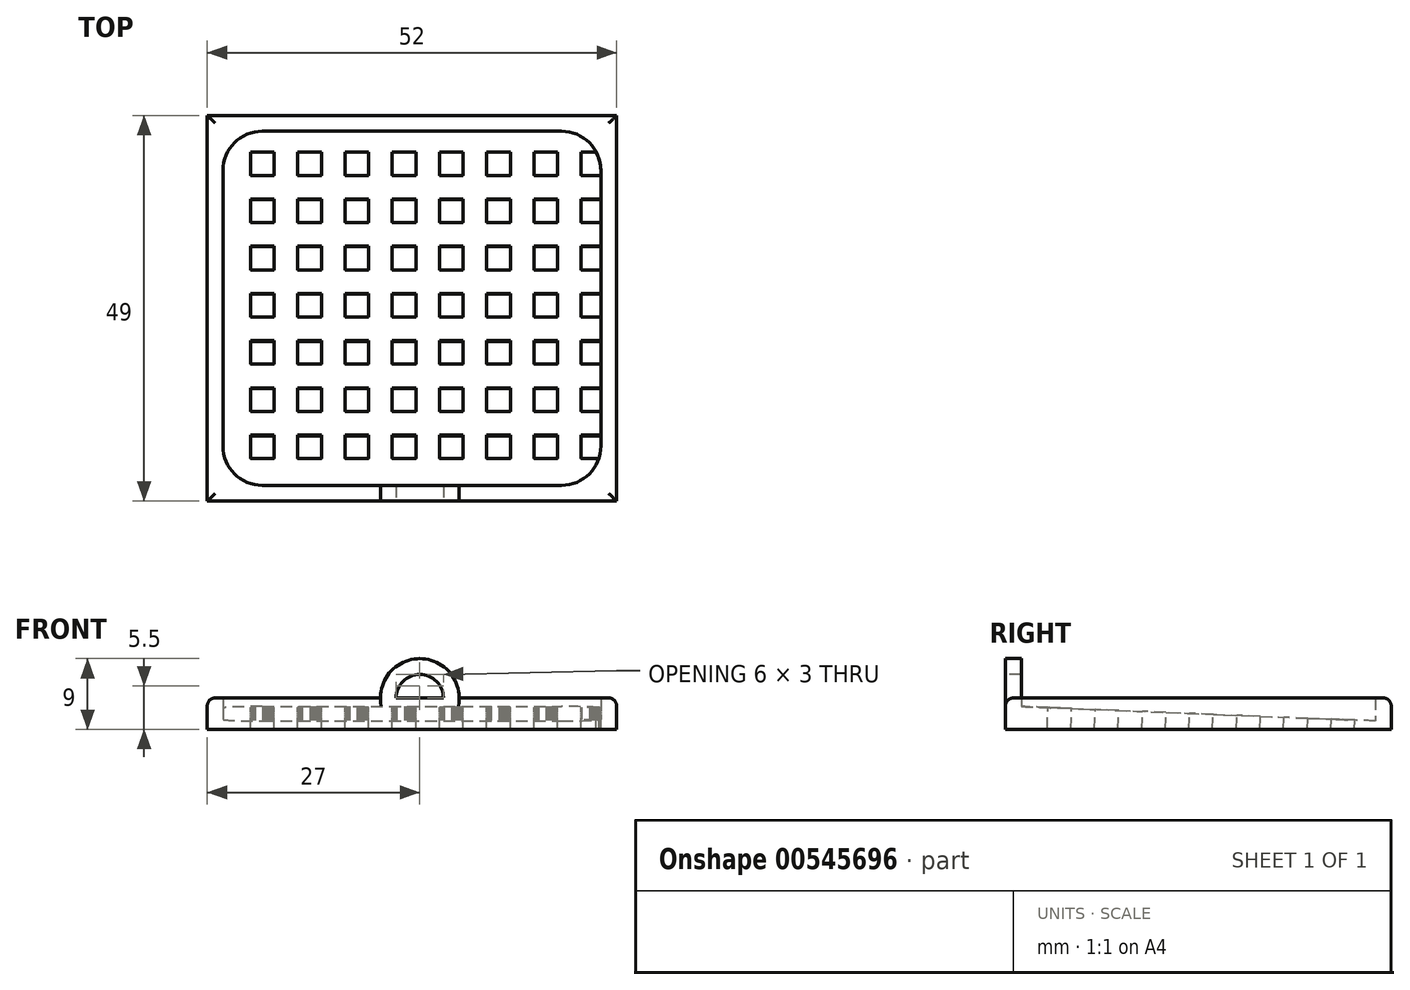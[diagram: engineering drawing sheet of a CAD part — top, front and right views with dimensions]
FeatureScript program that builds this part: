
annotation { "Feature Type Name" : "Feature", "Feature Type Description" : "" }
export const myFeature = defineFeature(function(context is Context, id is Id, definition is map)
    precondition{}
    {
        {
            var Q0;
            Q0=qCreatedBy(makeId("Top.planeOp"),FACE);
            var sketch = newSketch(context, id + "F0", { "sketchPlane" : qUnion([Q0])});
            skLineSegment(sketch, "E0.bottom", {"start": v(25, 24) * mm, "end": v(-27, 24) * mm});
            skLineSegment(sketch, "E0.top", {"start": v(25, -25) * mm, "end": v(-27, -25) * mm});
            skLineSegment(sketch, "E0.left", {"start": v(25, 24) * mm, "end": v(25, -25) * mm});
            skLineSegment(sketch, "E0.right", {"start": v(-27, 24) * mm, "end": v(-27, -25) * mm});
            skLineSegment(sketch, "E1", {"start": v(-24.88, -23) * mm, "end": v(-23.24, -21.45) * mm});
            skLineSegment(sketch, "E2.0", {"start": v(-23.42, -23) * mm, "end": v(-23.22, -22.82) * mm});
            skLineSegment(sketch, "E3.2.0.0", {"start": v(-14.88, -23) * mm, "end": v(-11.7, -20.01) * mm});
            skLineSegment(sketch, "E3.6.0.0", {"start": v(5.12, -23) * mm, "end": v(8.3, -20.01) * mm});
            skLineSegment(sketch, "E3.9.0.0", {"start": v(20.12, -23) * mm, "end": v(23, -20.29) * mm});
            skLineSegment(sketch, "E3.direction1", {"start": v(-27, -25) * mm, "end": v(-22, -25) * mm, "construction": true});
            skLineSegment(sketch, "E4.MirrorCS", {"start": v(-27, -20.37) * mm, "end": v(-26.7, -20) * mm});
            skLineSegment(sketch, "E5.MirrorCS", {"start": v(11.47, -26.5) * mm, "end": v(13.06, -25) * mm});
            skPoint(sketch, "E6.orphan", {"position": v(-24.94, 9.96) * mm});
            skPoint(sketch, "E7.orphan", {"position": v(-25.22, 4.95) * mm});
            skPoint(sketch, "E8.orphan", {"position": v(-25.54, -0.02) * mm});
            skPoint(sketch, "E9.orphan", {"position": v(28.1, 71.58) * mm});
            skPoint(sketch, "E10.orphan", {"position": v(27.67, 68.92) * mm});
            skPoint(sketch, "E11.orphan", {"position": v(27.8, 66.59) * mm});
            skPoint(sketch, "E12.orphan", {"position": v(27.37, 63.93) * mm});
            skPoint(sketch, "E13.orphan", {"position": v(27.5, 61.6) * mm});
            skPoint(sketch, "E14.orphan", {"position": v(27.08, 58.94) * mm});
            skPoint(sketch, "E15.orphan", {"position": v(27.2, 56.6) * mm});
            skPoint(sketch, "E16.orphan", {"position": v(26.78, 53.95) * mm});
            skPoint(sketch, "E17.orphan", {"position": v(26.9, 51.61) * mm});
            skPoint(sketch, "E18.orphan", {"position": v(26.48, 48.96) * mm});
            skPoint(sketch, "E19.orphan", {"position": v(26.61, 46.62) * mm});
            skPoint(sketch, "E20.orphan", {"position": v(26.19, 43.96) * mm});
            skPoint(sketch, "E21.orphan", {"position": v(28.15, 39.96) * mm});
            skPoint(sketch, "E22.orphan", {"position": v(27.44, 40.7) * mm});
            skPoint(sketch, "E23.orphan", {"position": v(27.06, 35.7) * mm});
            skPoint(sketch, "E24.orphan", {"position": v(27.77, 34.97) * mm});
            skPoint(sketch, "E25.MirrorCS.start.orphan", {"position": v(-12, -25) * mm});
            skPoint(sketch, "E26.orphan", {"position": v(45, 24) * mm});
            skPoint(sketch, "E27.orphan", {"position": v(47.68, 24.27) * mm});
            skPoint(sketch, "E28.orphan", {"position": v(50, 24) * mm});
            skPoint(sketch, "E3.5.0.0.start.orphan", {"position": v(-1.98, -25.03) * mm});
            skPoint(sketch, "E3.4.0.0.start.orphan", {"position": v(-6.99, -25.05) * mm});
            skPoint(sketch, "E29.orphan", {"position": v(52.68, 24.27) * mm});
            skPoint(sketch, "E30.orphan", {"position": v(55, 24) * mm});
            skPoint(sketch, "E31.MirrorCS.start.orphan", {"position": v(3, -25) * mm});
            skPoint(sketch, "E32.orphan", {"position": v(57.68, 24.27) * mm});
            skPoint(sketch, "E33.orphan", {"position": v(72.68, 24.27) * mm});
            skPoint(sketch, "E34.orphan", {"position": v(70, 24) * mm});
            skPoint(sketch, "E35.orphan", {"position": v(67.68, 24.27) * mm});
            skPoint(sketch, "E36.orphan", {"position": v(65, 24) * mm});
            skPoint(sketch, "E37.orphan", {"position": v(62.68, 24.27) * mm});
            skPoint(sketch, "E38.orphan", {"position": v(60, 24) * mm});
            skPoint(sketch, "E3.7.0.0.start.orphan", {"position": v(8.02, -25.02) * mm});
            skLineSegment(sketch, "E39", {"start": v(-4.84, -23) * mm, "end": v(-1.66, -19.97) * mm});
            skLineSegment(sketch, "E40.trimOffspring", {"start": v(16.63, -23) * mm, "end": v(18.34, -21.42) * mm});
            skLineSegment(sketch, "E41.trimOffspring", {"start": v(6.63, -23) * mm, "end": v(8.34, -21.42) * mm});
            skLineSegment(sketch, "E42.trimOffspring", {"start": v(-3.37, -23) * mm, "end": v(-1.66, -21.42) * mm});
            skLineSegment(sketch, "E43.trimOffspring", {"start": v(-13.37, -23) * mm, "end": v(-11.66, -21.42) * mm});
            skPoint(sketch, "E44.orphan", {"position": v(-30.63, -29.8) * mm});
            skPoint(sketch, "E45.orphan", {"position": v(-25.86, -5.02) * mm});
            skPoint(sketch, "E46.orphan", {"position": v(-26.1, -10.03) * mm});
            skPoint(sketch, "E47.orphan", {"position": v(-26.4, -15.02) * mm});
            skPoint(sketch, "E48.orphan", {"position": v(-26.7, -20) * mm});
            skLineSegment(sketch, "E49.0", {"start": v(18, 22) * mm, "end": v(-20, 22) * mm});
            skLineSegment(sketch, "E49.1", {"start": v(23, 17) * mm, "end": v(23, -18) * mm});
            skLineSegment(sketch, "E49.2", {"start": v(18, -23) * mm, "end": v(-20, -23) * mm});
            skLineSegment(sketch, "E49.3", {"start": v(-25, 17) * mm, "end": v(-25, -18) * mm});
            skPoint(sketch, "E50.orphan", {"position": v(-22, -25) * mm});
            skPoint(sketch, "E51.orphan", {"position": v(-17, -25) * mm});
            skLineSegment(sketch, "E52.trimOffspring", {"start": v(15.18, -23) * mm, "end": v(16.74, -21.53) * mm});
            skPoint(sketch, "E53.orphan", {"position": v(18, -25) * mm});
            skLineSegment(sketch, "E54.bottom", {"start": v(-11.66, 22) * mm, "end": v(-9.84, 22) * mm});
            skLineSegment(sketch, "E54.top", {"start": v(-11.66, -23) * mm, "end": v(-9.84, -23) * mm});
            skLineSegment(sketch, "E55.bottom", {"start": v(-1.66, 22) * mm, "end": v(0.21, 22) * mm});
            skLineSegment(sketch, "E55.top", {"start": v(-1.66, -23) * mm, "end": v(0.21, -23) * mm});
            skLineSegment(sketch, "E56.bottom", {"start": v(8.34, 22) * mm, "end": v(10.2, 22) * mm});
            skLineSegment(sketch, "E56.top", {"start": v(8.34, -23) * mm, "end": v(10.2, -23) * mm});
            skLineSegment(sketch, "E57.bottom", {"start": v(18.34, 22) * mm, "end": v(20.16, 22) * mm});
            skLineSegment(sketch, "E57.top", {"start": v(18.34, -23) * mm, "end": v(20.12, -23) * mm});
            skLineSegment(sketch, "E58.bottom", {"start": v(-21.63, 22) * mm, "end": v(-19.84, 22) * mm});
            skLineSegment(sketch, "E58.top", {"start": v(-21.63, -23) * mm, "end": v(-19.84, -23) * mm});
            skPoint(sketch, "E59.visualSharp", {"position": v(-25, 22) * mm});
            skArc(sketch, "E59.filletArc", {"start": v(-20, 22) * mm, "mid": v(-23.54, 20.54) * mm, "end": v(-25, 17) * mm});
            skPoint(sketch, "E60.visualSharp", {"position": v(23, 22) * mm});
            skArc(sketch, "E60.filletArc", {"start": v(23, 17) * mm, "mid": v(21.54, 20.54) * mm, "end": v(18, 22) * mm});
            skPoint(sketch, "E61.visualSharp", {"position": v(-25, -23) * mm});
            skArc(sketch, "E61.filletArc", {"start": v(-25, -18) * mm, "mid": v(-23.54, -21.54) * mm, "end": v(-20, -23) * mm});
            skPoint(sketch, "E62.visualSharp", {"position": v(23, -23) * mm});
            skArc(sketch, "E62.filletArc", {"start": v(18, -23) * mm, "mid": v(21.54, -21.54) * mm, "end": v(23, -18) * mm});
            skLineSegment(sketch, "E63.trimOffspring", {"start": v(20.16, 20.4) * mm, "end": v(21.9, 22) * mm});
            skSolve(sketch);
        }
        {
            var Q0;
            {var subQ117=sQuery(id+"F0.wireOp",EDGE,"E0.bottom");Q0=makeQuery(id+"F0.imprint","IMPRINT",FACE,{"disambiguationData":[TD([[makeQuery(id+"F0.imprint","IMPRINT",EDGE,{"derivedFrom":subQ117}),1.0]])]});}
            extrude(context, id + "F1", {"entities" : qUnion([Q0]), "depth" : 4 * mm, "offsetDistance" : 25 * mm});
        }
        {
            var Q0;
            Q0=makeQuery(id+"F1.opExtrude","SWEPT_FACE",FACE,{"disambiguationData":[OSD([sQuery(id+"F0.wireOp",EDGE,"E0.left")])]});
            var sketch = newSketch(context, id + "F2", { "sketchPlane" : qUnion([Q0])});
            skLineSegment(sketch, "E64.0.0", {"start": v(-25, 0) * mm, "end": v(24, 0) * mm});
            skLineSegment(sketch, "E64.0.1", {"start": v(24, 0) * mm, "end": v(24, 4) * mm});
            skLineSegment(sketch, "E64.0.2", {"start": v(24, 4) * mm, "end": v(-25, 4) * mm});
            skLineSegment(sketch, "E64.0.3", {"start": v(-25, 4) * mm, "end": v(-25, 0) * mm});
            skPoint(sketch, "E65", {"position": v(24, 1) * mm});
            skLineSegment(sketch, "E66", {"start": v(3.74, 1.65) * mm, "end": v(4.17, 1.62) * mm});
            skLineSegment(sketch, "E67", {"start": v(24, 0) * mm, "end": v(24, 1) * mm});
            skLineSegment(sketch, "E68", {"start": v(-25, 4) * mm, "end": v(-25, 3) * mm});
            skLineSegment(sketch, "E69", {"start": v(-25, 3) * mm, "end": v(24, 1) * mm});
            skSolve(sketch);
        }
        {
            var Q0;
            {var subQ0=sQuery(id+"F2.wireOp",EDGE,"E64.0.0");Q0=makeQuery(id+"F2.imprint","IMPRINT",FACE,{"disambiguationData":[TD([[makeQuery(id+"F2.imprint","IMPRINT",EDGE,{"derivedFrom":subQ0}),-1.0]])]});}
            extrude(context, id + "F3", {"entities" : qUnion([Q0]), "operationType" : NewBodyOperationType.ADD, "oppositeDirection" : true, "depth" : 51 * mm, "offsetDistance" : 25 * mm});
        }
        {
            var Q0;
            Q0=makeQuery(id+"F3.opExtrude","SWEPT_FACE",FACE,{"disambiguationData":[OSD([sQuery(id+"F2.wireOp",EDGE,"E69")])]});
            var sketch = newSketch(context, id + "F4", { "sketchPlane" : qUnion([Q0])});
            skLineSegment(sketch, "E70.0.0", {"start": v(-20, -23.2) * mm, "end": v(18, -23.2) * mm});
            skEllipticalArc(sketch, "E70.0.1", {});
            skLineSegment(sketch, "E70.0.2", {"start": v(23, -18.18) * mm, "end": v(23, 16.88) * mm});
            skEllipticalArc(sketch, "E70.0.3", {});
            skLineSegment(sketch, "E70.0.4", {"start": v(18, 21.9) * mm, "end": v(-20, 21.9) * mm});
            skEllipticalArc(sketch, "E70.0.5", {});
            skLineSegment(sketch, "E70.0.6", {"start": v(-25, 16.88) * mm, "end": v(-25, -18.18) * mm});
            skEllipticalArc(sketch, "E70.0.7", {});
            skLineSegment(sketch, "E71.bottom", {"start": v(-18.5, -16.68) * mm, "end": v(-21.5, -16.68) * mm});
            skLineSegment(sketch, "E71.top", {"start": v(-18.5, -19.68) * mm, "end": v(-21.5, -19.68) * mm});
            skLineSegment(sketch, "E71.left", {"start": v(-18.5, -16.68) * mm, "end": v(-18.5, -19.68) * mm});
            skLineSegment(sketch, "E71.right", {"start": v(-21.5, -16.68) * mm, "end": v(-21.5, -19.68) * mm});
            skLineSegment(sketch, "E72.0.1.0", {"start": v(-21.5, -10.68) * mm, "end": v(-21.5, -13.68) * mm});
            skLineSegment(sketch, "E72.0.1.1", {"start": v(-18.5, -10.68) * mm, "end": v(-21.5, -10.68) * mm});
            skLineSegment(sketch, "E72.0.1.2", {"start": v(-18.5, -10.68) * mm, "end": v(-18.5, -13.68) * mm});
            skLineSegment(sketch, "E72.0.1.3", {"start": v(-18.5, -13.68) * mm, "end": v(-21.5, -13.68) * mm});
            skLineSegment(sketch, "E72.0.2.0", {"start": v(-21.5, -4.68) * mm, "end": v(-21.5, -7.68) * mm});
            skLineSegment(sketch, "E72.0.2.1", {"start": v(-18.5, -4.68) * mm, "end": v(-21.5, -4.68) * mm});
            skLineSegment(sketch, "E72.0.2.2", {"start": v(-18.5, -4.68) * mm, "end": v(-18.5, -7.68) * mm});
            skLineSegment(sketch, "E72.0.2.3", {"start": v(-18.5, -7.68) * mm, "end": v(-21.5, -7.68) * mm});
            skLineSegment(sketch, "E72.0.3.0", {"start": v(-21.5, 1.32) * mm, "end": v(-21.5, -1.68) * mm});
            skLineSegment(sketch, "E72.0.3.1", {"start": v(-18.5, 1.32) * mm, "end": v(-21.5, 1.32) * mm});
            skLineSegment(sketch, "E72.0.3.2", {"start": v(-18.5, 1.32) * mm, "end": v(-18.5, -1.68) * mm});
            skLineSegment(sketch, "E72.0.3.3", {"start": v(-18.5, -1.68) * mm, "end": v(-21.5, -1.68) * mm});
            skLineSegment(sketch, "E72.0.4.0", {"start": v(-21.5, 7.32) * mm, "end": v(-21.5, 4.32) * mm});
            skLineSegment(sketch, "E72.0.4.1", {"start": v(-18.5, 7.32) * mm, "end": v(-21.5, 7.32) * mm});
            skLineSegment(sketch, "E72.0.4.2", {"start": v(-18.5, 7.32) * mm, "end": v(-18.5, 4.32) * mm});
            skLineSegment(sketch, "E72.0.4.3", {"start": v(-18.5, 4.32) * mm, "end": v(-21.5, 4.32) * mm});
            skLineSegment(sketch, "E72.0.5.0", {"start": v(-21.5, 13.32) * mm, "end": v(-21.5, 10.32) * mm});
            skLineSegment(sketch, "E72.0.5.1", {"start": v(-18.5, 13.32) * mm, "end": v(-21.5, 13.32) * mm});
            skLineSegment(sketch, "E72.0.5.2", {"start": v(-18.5, 13.32) * mm, "end": v(-18.5, 10.32) * mm});
            skLineSegment(sketch, "E72.0.5.3", {"start": v(-18.5, 10.32) * mm, "end": v(-21.5, 10.32) * mm});
            skLineSegment(sketch, "E72.0.6.0", {"start": v(-21.5, 19.32) * mm, "end": v(-21.5, 16.32) * mm});
            skLineSegment(sketch, "E72.0.6.1", {"start": v(-18.5, 19.32) * mm, "end": v(-21.5, 19.32) * mm});
            skLineSegment(sketch, "E72.0.6.2", {"start": v(-18.5, 19.32) * mm, "end": v(-18.5, 16.32) * mm});
            skLineSegment(sketch, "E72.0.6.3", {"start": v(-18.5, 16.32) * mm, "end": v(-21.5, 16.32) * mm});
            skLineSegment(sketch, "E72.1.0.0", {"start": v(-15.5, -16.68) * mm, "end": v(-15.5, -19.68) * mm});
            skLineSegment(sketch, "E72.1.0.1", {"start": v(-12.5, -16.68) * mm, "end": v(-15.5, -16.68) * mm});
            skLineSegment(sketch, "E72.1.0.2", {"start": v(-12.5, -16.68) * mm, "end": v(-12.5, -19.68) * mm});
            skLineSegment(sketch, "E72.1.0.3", {"start": v(-12.5, -19.68) * mm, "end": v(-15.5, -19.68) * mm});
            skLineSegment(sketch, "E72.1.1.0", {"start": v(-15.5, -10.68) * mm, "end": v(-15.5, -13.68) * mm});
            skLineSegment(sketch, "E72.1.1.1", {"start": v(-12.5, -10.68) * mm, "end": v(-15.5, -10.68) * mm});
            skLineSegment(sketch, "E72.1.1.2", {"start": v(-12.5, -10.68) * mm, "end": v(-12.5, -13.68) * mm});
            skLineSegment(sketch, "E72.1.1.3", {"start": v(-12.5, -13.68) * mm, "end": v(-15.5, -13.68) * mm});
            skLineSegment(sketch, "E72.1.2.0", {"start": v(-15.5, -4.68) * mm, "end": v(-15.5, -7.68) * mm});
            skLineSegment(sketch, "E72.1.2.1", {"start": v(-12.5, -4.68) * mm, "end": v(-15.5, -4.68) * mm});
            skLineSegment(sketch, "E72.1.2.2", {"start": v(-12.5, -4.68) * mm, "end": v(-12.5, -7.68) * mm});
            skLineSegment(sketch, "E72.1.2.3", {"start": v(-12.5, -7.68) * mm, "end": v(-15.5, -7.68) * mm});
            skLineSegment(sketch, "E72.1.3.0", {"start": v(-15.5, 1.32) * mm, "end": v(-15.5, -1.68) * mm});
            skLineSegment(sketch, "E72.1.3.1", {"start": v(-12.5, 1.32) * mm, "end": v(-15.5, 1.32) * mm});
            skLineSegment(sketch, "E72.1.3.2", {"start": v(-12.5, 1.32) * mm, "end": v(-12.5, -1.68) * mm});
            skLineSegment(sketch, "E72.1.3.3", {"start": v(-12.5, -1.68) * mm, "end": v(-15.5, -1.68) * mm});
            skLineSegment(sketch, "E72.1.4.0", {"start": v(-15.5, 7.32) * mm, "end": v(-15.5, 4.32) * mm});
            skLineSegment(sketch, "E72.1.4.1", {"start": v(-12.5, 7.32) * mm, "end": v(-15.5, 7.32) * mm});
            skLineSegment(sketch, "E72.1.4.2", {"start": v(-12.5, 7.32) * mm, "end": v(-12.5, 4.32) * mm});
            skLineSegment(sketch, "E72.1.4.3", {"start": v(-12.5, 4.32) * mm, "end": v(-15.5, 4.32) * mm});
            skLineSegment(sketch, "E72.1.5.0", {"start": v(-15.5, 13.32) * mm, "end": v(-15.5, 10.32) * mm});
            skLineSegment(sketch, "E72.1.5.1", {"start": v(-12.5, 13.32) * mm, "end": v(-15.5, 13.32) * mm});
            skLineSegment(sketch, "E72.1.5.2", {"start": v(-12.5, 13.32) * mm, "end": v(-12.5, 10.32) * mm});
            skLineSegment(sketch, "E72.1.5.3", {"start": v(-12.5, 10.32) * mm, "end": v(-15.5, 10.32) * mm});
            skLineSegment(sketch, "E72.1.6.0", {"start": v(-15.5, 19.32) * mm, "end": v(-15.5, 16.32) * mm});
            skLineSegment(sketch, "E72.1.6.1", {"start": v(-12.5, 19.32) * mm, "end": v(-15.5, 19.32) * mm});
            skLineSegment(sketch, "E72.1.6.2", {"start": v(-12.5, 19.32) * mm, "end": v(-12.5, 16.32) * mm});
            skLineSegment(sketch, "E72.1.6.3", {"start": v(-12.5, 16.32) * mm, "end": v(-15.5, 16.32) * mm});
            skLineSegment(sketch, "E72.2.0.0", {"start": v(-9.5, -16.68) * mm, "end": v(-9.5, -19.68) * mm});
            skLineSegment(sketch, "E72.2.0.1", {"start": v(-6.5, -16.68) * mm, "end": v(-9.5, -16.68) * mm});
            skLineSegment(sketch, "E72.2.0.2", {"start": v(-6.5, -16.68) * mm, "end": v(-6.5, -19.68) * mm});
            skLineSegment(sketch, "E72.2.0.3", {"start": v(-6.5, -19.68) * mm, "end": v(-9.5, -19.68) * mm});
            skLineSegment(sketch, "E72.2.1.0", {"start": v(-9.5, -10.68) * mm, "end": v(-9.5, -13.68) * mm});
            skLineSegment(sketch, "E72.2.1.1", {"start": v(-6.5, -10.68) * mm, "end": v(-9.5, -10.68) * mm});
            skLineSegment(sketch, "E72.2.1.2", {"start": v(-6.5, -10.68) * mm, "end": v(-6.5, -13.68) * mm});
            skLineSegment(sketch, "E72.2.1.3", {"start": v(-6.5, -13.68) * mm, "end": v(-9.5, -13.68) * mm});
            skLineSegment(sketch, "E72.2.2.0", {"start": v(-9.5, -4.68) * mm, "end": v(-9.5, -7.68) * mm});
            skLineSegment(sketch, "E72.2.2.1", {"start": v(-6.5, -4.68) * mm, "end": v(-9.5, -4.68) * mm});
            skLineSegment(sketch, "E72.2.2.2", {"start": v(-6.5, -4.68) * mm, "end": v(-6.5, -7.68) * mm});
            skLineSegment(sketch, "E72.2.2.3", {"start": v(-6.5, -7.68) * mm, "end": v(-9.5, -7.68) * mm});
            skLineSegment(sketch, "E72.2.3.0", {"start": v(-9.5, 1.32) * mm, "end": v(-9.5, -1.68) * mm});
            skLineSegment(sketch, "E72.2.3.1", {"start": v(-6.5, 1.32) * mm, "end": v(-9.5, 1.32) * mm});
            skLineSegment(sketch, "E72.2.3.2", {"start": v(-6.5, 1.32) * mm, "end": v(-6.5, -1.68) * mm});
            skLineSegment(sketch, "E72.2.3.3", {"start": v(-6.5, -1.68) * mm, "end": v(-9.5, -1.68) * mm});
            skLineSegment(sketch, "E72.2.4.0", {"start": v(-9.5, 7.32) * mm, "end": v(-9.5, 4.32) * mm});
            skLineSegment(sketch, "E72.2.4.1", {"start": v(-6.5, 7.32) * mm, "end": v(-9.5, 7.32) * mm});
            skLineSegment(sketch, "E72.2.4.2", {"start": v(-6.5, 7.32) * mm, "end": v(-6.5, 4.32) * mm});
            skLineSegment(sketch, "E72.2.4.3", {"start": v(-6.5, 4.32) * mm, "end": v(-9.5, 4.32) * mm});
            skLineSegment(sketch, "E72.2.5.0", {"start": v(-9.5, 13.32) * mm, "end": v(-9.5, 10.32) * mm});
            skLineSegment(sketch, "E72.2.5.1", {"start": v(-6.5, 13.32) * mm, "end": v(-9.5, 13.32) * mm});
            skLineSegment(sketch, "E72.2.5.2", {"start": v(-6.5, 13.32) * mm, "end": v(-6.5, 10.32) * mm});
            skLineSegment(sketch, "E72.2.5.3", {"start": v(-6.5, 10.32) * mm, "end": v(-9.5, 10.32) * mm});
            skLineSegment(sketch, "E72.2.6.0", {"start": v(-9.5, 19.32) * mm, "end": v(-9.5, 16.32) * mm});
            skLineSegment(sketch, "E72.2.6.1", {"start": v(-6.5, 19.32) * mm, "end": v(-9.5, 19.32) * mm});
            skLineSegment(sketch, "E72.2.6.2", {"start": v(-6.5, 19.32) * mm, "end": v(-6.5, 16.32) * mm});
            skLineSegment(sketch, "E72.2.6.3", {"start": v(-6.5, 16.32) * mm, "end": v(-9.5, 16.32) * mm});
            skLineSegment(sketch, "E72.3.0.0", {"start": v(-3.5, -16.68) * mm, "end": v(-3.5, -19.68) * mm});
            skLineSegment(sketch, "E72.3.0.1", {"start": v(-0.5, -16.68) * mm, "end": v(-3.5, -16.68) * mm});
            skLineSegment(sketch, "E72.3.0.2", {"start": v(-0.5, -16.68) * mm, "end": v(-0.5, -19.68) * mm});
            skLineSegment(sketch, "E72.3.0.3", {"start": v(-0.5, -19.68) * mm, "end": v(-3.5, -19.68) * mm});
            skLineSegment(sketch, "E72.3.1.0", {"start": v(-3.5, -10.68) * mm, "end": v(-3.5, -13.68) * mm});
            skLineSegment(sketch, "E72.3.1.1", {"start": v(-0.5, -10.68) * mm, "end": v(-3.5, -10.68) * mm});
            skLineSegment(sketch, "E72.3.1.2", {"start": v(-0.5, -10.68) * mm, "end": v(-0.5, -13.68) * mm});
            skLineSegment(sketch, "E72.3.1.3", {"start": v(-0.5, -13.68) * mm, "end": v(-3.5, -13.68) * mm});
            skLineSegment(sketch, "E72.3.2.0", {"start": v(-3.5, -4.68) * mm, "end": v(-3.5, -7.68) * mm});
            skLineSegment(sketch, "E72.3.2.1", {"start": v(-0.5, -4.68) * mm, "end": v(-3.5, -4.68) * mm});
            skLineSegment(sketch, "E72.3.2.2", {"start": v(-0.5, -4.68) * mm, "end": v(-0.5, -7.68) * mm});
            skLineSegment(sketch, "E72.3.2.3", {"start": v(-0.5, -7.68) * mm, "end": v(-3.5, -7.68) * mm});
            skLineSegment(sketch, "E72.3.3.0", {"start": v(-3.5, 1.32) * mm, "end": v(-3.5, -1.68) * mm});
            skLineSegment(sketch, "E72.3.3.1", {"start": v(-0.5, 1.32) * mm, "end": v(-3.5, 1.32) * mm});
            skLineSegment(sketch, "E72.3.3.2", {"start": v(-0.5, 1.32) * mm, "end": v(-0.5, -1.68) * mm});
            skLineSegment(sketch, "E72.3.3.3", {"start": v(-0.5, -1.68) * mm, "end": v(-3.5, -1.68) * mm});
            skLineSegment(sketch, "E72.3.4.0", {"start": v(-3.5, 7.32) * mm, "end": v(-3.5, 4.32) * mm});
            skLineSegment(sketch, "E72.3.4.1", {"start": v(-0.5, 7.32) * mm, "end": v(-3.5, 7.32) * mm});
            skLineSegment(sketch, "E72.3.4.2", {"start": v(-0.5, 7.32) * mm, "end": v(-0.5, 4.32) * mm});
            skLineSegment(sketch, "E72.3.4.3", {"start": v(-0.5, 4.32) * mm, "end": v(-3.5, 4.32) * mm});
            skLineSegment(sketch, "E72.3.5.0", {"start": v(-3.5, 13.32) * mm, "end": v(-3.5, 10.32) * mm});
            skLineSegment(sketch, "E72.3.5.1", {"start": v(-0.5, 13.32) * mm, "end": v(-3.5, 13.32) * mm});
            skLineSegment(sketch, "E72.3.5.2", {"start": v(-0.5, 13.32) * mm, "end": v(-0.5, 10.32) * mm});
            skLineSegment(sketch, "E72.3.5.3", {"start": v(-0.5, 10.32) * mm, "end": v(-3.5, 10.32) * mm});
            skLineSegment(sketch, "E72.3.6.0", {"start": v(-3.5, 19.32) * mm, "end": v(-3.5, 16.32) * mm});
            skLineSegment(sketch, "E72.3.6.1", {"start": v(-0.5, 19.32) * mm, "end": v(-3.5, 19.32) * mm});
            skLineSegment(sketch, "E72.3.6.2", {"start": v(-0.5, 19.32) * mm, "end": v(-0.5, 16.32) * mm});
            skLineSegment(sketch, "E72.3.6.3", {"start": v(-0.5, 16.32) * mm, "end": v(-3.5, 16.32) * mm});
            skLineSegment(sketch, "E72.4.0.0", {"start": v(2.5, -16.68) * mm, "end": v(2.5, -19.68) * mm});
            skLineSegment(sketch, "E72.4.0.1", {"start": v(5.5, -16.68) * mm, "end": v(2.5, -16.68) * mm});
            skLineSegment(sketch, "E72.4.0.2", {"start": v(5.5, -16.68) * mm, "end": v(5.5, -19.68) * mm});
            skLineSegment(sketch, "E72.4.0.3", {"start": v(5.5, -19.68) * mm, "end": v(2.5, -19.68) * mm});
            skLineSegment(sketch, "E72.4.1.0", {"start": v(2.5, -10.68) * mm, "end": v(2.5, -13.68) * mm});
            skLineSegment(sketch, "E72.4.1.1", {"start": v(5.5, -10.68) * mm, "end": v(2.5, -10.68) * mm});
            skLineSegment(sketch, "E72.4.1.2", {"start": v(5.5, -10.68) * mm, "end": v(5.5, -13.68) * mm});
            skLineSegment(sketch, "E72.4.1.3", {"start": v(5.5, -13.68) * mm, "end": v(2.5, -13.68) * mm});
            skLineSegment(sketch, "E72.4.2.0", {"start": v(2.5, -4.68) * mm, "end": v(2.5, -7.68) * mm});
            skLineSegment(sketch, "E72.4.2.1", {"start": v(5.5, -4.68) * mm, "end": v(2.5, -4.68) * mm});
            skLineSegment(sketch, "E72.4.2.2", {"start": v(5.5, -4.68) * mm, "end": v(5.5, -7.68) * mm});
            skLineSegment(sketch, "E72.4.2.3", {"start": v(5.5, -7.68) * mm, "end": v(2.5, -7.68) * mm});
            skLineSegment(sketch, "E72.4.3.0", {"start": v(2.5, 1.32) * mm, "end": v(2.5, -1.68) * mm});
            skLineSegment(sketch, "E72.4.3.1", {"start": v(5.5, 1.32) * mm, "end": v(2.5, 1.32) * mm});
            skLineSegment(sketch, "E72.4.3.2", {"start": v(5.5, 1.32) * mm, "end": v(5.5, -1.68) * mm});
            skLineSegment(sketch, "E72.4.3.3", {"start": v(5.5, -1.68) * mm, "end": v(2.5, -1.68) * mm});
            skLineSegment(sketch, "E72.4.4.0", {"start": v(2.5, 7.32) * mm, "end": v(2.5, 4.32) * mm});
            skLineSegment(sketch, "E72.4.4.1", {"start": v(5.5, 7.32) * mm, "end": v(2.5, 7.32) * mm});
            skLineSegment(sketch, "E72.4.4.2", {"start": v(5.5, 7.32) * mm, "end": v(5.5, 4.32) * mm});
            skLineSegment(sketch, "E72.4.4.3", {"start": v(5.5, 4.32) * mm, "end": v(2.5, 4.32) * mm});
            skLineSegment(sketch, "E72.4.5.0", {"start": v(2.5, 13.32) * mm, "end": v(2.5, 10.32) * mm});
            skLineSegment(sketch, "E72.4.5.1", {"start": v(5.5, 13.32) * mm, "end": v(2.5, 13.32) * mm});
            skLineSegment(sketch, "E72.4.5.2", {"start": v(5.5, 13.32) * mm, "end": v(5.5, 10.32) * mm});
            skLineSegment(sketch, "E72.4.5.3", {"start": v(5.5, 10.32) * mm, "end": v(2.5, 10.32) * mm});
            skLineSegment(sketch, "E72.4.6.0", {"start": v(2.5, 19.32) * mm, "end": v(2.5, 16.32) * mm});
            skLineSegment(sketch, "E72.4.6.1", {"start": v(5.5, 19.32) * mm, "end": v(2.5, 19.32) * mm});
            skLineSegment(sketch, "E72.4.6.2", {"start": v(5.5, 19.32) * mm, "end": v(5.5, 16.32) * mm});
            skLineSegment(sketch, "E72.4.6.3", {"start": v(5.5, 16.32) * mm, "end": v(2.5, 16.32) * mm});
            skLineSegment(sketch, "E72.5.0.0", {"start": v(8.5, -16.68) * mm, "end": v(8.5, -19.68) * mm});
            skLineSegment(sketch, "E72.5.0.1", {"start": v(11.5, -16.68) * mm, "end": v(8.5, -16.68) * mm});
            skLineSegment(sketch, "E72.5.0.2", {"start": v(11.5, -16.68) * mm, "end": v(11.5, -19.68) * mm});
            skLineSegment(sketch, "E72.5.0.3", {"start": v(11.5, -19.68) * mm, "end": v(8.5, -19.68) * mm});
            skLineSegment(sketch, "E72.5.1.0", {"start": v(8.5, -10.68) * mm, "end": v(8.5, -13.68) * mm});
            skLineSegment(sketch, "E72.5.1.1", {"start": v(11.5, -10.68) * mm, "end": v(8.5, -10.68) * mm});
            skLineSegment(sketch, "E72.5.1.2", {"start": v(11.5, -10.68) * mm, "end": v(11.5, -13.68) * mm});
            skLineSegment(sketch, "E72.5.1.3", {"start": v(11.5, -13.68) * mm, "end": v(8.5, -13.68) * mm});
            skLineSegment(sketch, "E72.5.2.0", {"start": v(8.5, -4.68) * mm, "end": v(8.5, -7.68) * mm});
            skLineSegment(sketch, "E72.5.2.1", {"start": v(11.5, -4.68) * mm, "end": v(8.5, -4.68) * mm});
            skLineSegment(sketch, "E72.5.2.2", {"start": v(11.5, -4.68) * mm, "end": v(11.5, -7.68) * mm});
            skLineSegment(sketch, "E72.5.2.3", {"start": v(11.5, -7.68) * mm, "end": v(8.5, -7.68) * mm});
            skLineSegment(sketch, "E72.5.3.0", {"start": v(8.5, 1.32) * mm, "end": v(8.5, -1.68) * mm});
            skLineSegment(sketch, "E72.5.3.1", {"start": v(11.5, 1.32) * mm, "end": v(8.5, 1.32) * mm});
            skLineSegment(sketch, "E72.5.3.2", {"start": v(11.5, 1.32) * mm, "end": v(11.5, -1.68) * mm});
            skLineSegment(sketch, "E72.5.3.3", {"start": v(11.5, -1.68) * mm, "end": v(8.5, -1.68) * mm});
            skLineSegment(sketch, "E72.5.4.0", {"start": v(8.5, 7.32) * mm, "end": v(8.5, 4.32) * mm});
            skLineSegment(sketch, "E72.5.4.1", {"start": v(11.5, 7.32) * mm, "end": v(8.5, 7.32) * mm});
            skLineSegment(sketch, "E72.5.4.2", {"start": v(11.5, 7.32) * mm, "end": v(11.5, 4.32) * mm});
            skLineSegment(sketch, "E72.5.4.3", {"start": v(11.5, 4.32) * mm, "end": v(8.5, 4.32) * mm});
            skLineSegment(sketch, "E72.5.5.0", {"start": v(8.5, 13.32) * mm, "end": v(8.5, 10.32) * mm});
            skLineSegment(sketch, "E72.5.5.1", {"start": v(11.5, 13.32) * mm, "end": v(8.5, 13.32) * mm});
            skLineSegment(sketch, "E72.5.5.2", {"start": v(11.5, 13.32) * mm, "end": v(11.5, 10.32) * mm});
            skLineSegment(sketch, "E72.5.5.3", {"start": v(11.5, 10.32) * mm, "end": v(8.5, 10.32) * mm});
            skLineSegment(sketch, "E72.5.6.0", {"start": v(8.5, 19.32) * mm, "end": v(8.5, 16.32) * mm});
            skLineSegment(sketch, "E72.5.6.1", {"start": v(11.5, 19.32) * mm, "end": v(8.5, 19.32) * mm});
            skLineSegment(sketch, "E72.5.6.2", {"start": v(11.5, 19.32) * mm, "end": v(11.5, 16.32) * mm});
            skLineSegment(sketch, "E72.5.6.3", {"start": v(11.5, 16.32) * mm, "end": v(8.5, 16.32) * mm});
            skLineSegment(sketch, "E72.6.0.0", {"start": v(14.5, -16.68) * mm, "end": v(14.5, -19.68) * mm});
            skLineSegment(sketch, "E72.6.0.1", {"start": v(17.5, -16.68) * mm, "end": v(14.5, -16.68) * mm});
            skLineSegment(sketch, "E72.6.0.2", {"start": v(17.5, -16.68) * mm, "end": v(17.5, -19.68) * mm});
            skLineSegment(sketch, "E72.6.0.3", {"start": v(17.5, -19.68) * mm, "end": v(14.5, -19.68) * mm});
            skLineSegment(sketch, "E72.6.1.0", {"start": v(14.5, -10.68) * mm, "end": v(14.5, -13.68) * mm});
            skLineSegment(sketch, "E72.6.1.1", {"start": v(17.5, -10.68) * mm, "end": v(14.5, -10.68) * mm});
            skLineSegment(sketch, "E72.6.1.2", {"start": v(17.5, -10.68) * mm, "end": v(17.5, -13.68) * mm});
            skLineSegment(sketch, "E72.6.1.3", {"start": v(17.5, -13.68) * mm, "end": v(14.5, -13.68) * mm});
            skLineSegment(sketch, "E72.6.2.0", {"start": v(14.5, -4.68) * mm, "end": v(14.5, -7.68) * mm});
            skLineSegment(sketch, "E72.6.2.1", {"start": v(17.5, -4.68) * mm, "end": v(14.5, -4.68) * mm});
            skLineSegment(sketch, "E72.6.2.2", {"start": v(17.5, -4.68) * mm, "end": v(17.5, -7.68) * mm});
            skLineSegment(sketch, "E72.6.2.3", {"start": v(17.5, -7.68) * mm, "end": v(14.5, -7.68) * mm});
            skLineSegment(sketch, "E72.6.3.0", {"start": v(14.5, 1.32) * mm, "end": v(14.5, -1.68) * mm});
            skLineSegment(sketch, "E72.6.3.1", {"start": v(17.5, 1.32) * mm, "end": v(14.5, 1.32) * mm});
            skLineSegment(sketch, "E72.6.3.2", {"start": v(17.5, 1.32) * mm, "end": v(17.5, -1.68) * mm});
            skLineSegment(sketch, "E72.6.3.3", {"start": v(17.5, -1.68) * mm, "end": v(14.5, -1.68) * mm});
            skLineSegment(sketch, "E72.6.4.0", {"start": v(14.5, 7.32) * mm, "end": v(14.5, 4.32) * mm});
            skLineSegment(sketch, "E72.6.4.1", {"start": v(17.5, 7.32) * mm, "end": v(14.5, 7.32) * mm});
            skLineSegment(sketch, "E72.6.4.2", {"start": v(17.5, 7.32) * mm, "end": v(17.5, 4.32) * mm});
            skLineSegment(sketch, "E72.6.4.3", {"start": v(17.5, 4.32) * mm, "end": v(14.5, 4.32) * mm});
            skLineSegment(sketch, "E72.6.5.0", {"start": v(14.5, 13.32) * mm, "end": v(14.5, 10.32) * mm});
            skLineSegment(sketch, "E72.6.5.1", {"start": v(17.5, 13.32) * mm, "end": v(14.5, 13.32) * mm});
            skLineSegment(sketch, "E72.6.5.2", {"start": v(17.5, 13.32) * mm, "end": v(17.5, 10.32) * mm});
            skLineSegment(sketch, "E72.6.5.3", {"start": v(17.5, 10.32) * mm, "end": v(14.5, 10.32) * mm});
            skLineSegment(sketch, "E72.6.6.0", {"start": v(14.5, 19.32) * mm, "end": v(14.5, 16.32) * mm});
            skLineSegment(sketch, "E72.6.6.1", {"start": v(17.5, 19.32) * mm, "end": v(14.5, 19.32) * mm});
            skLineSegment(sketch, "E72.6.6.2", {"start": v(17.5, 19.32) * mm, "end": v(17.5, 16.32) * mm});
            skLineSegment(sketch, "E72.6.6.3", {"start": v(17.5, 16.32) * mm, "end": v(14.5, 16.32) * mm});
            skLineSegment(sketch, "E72.7.0.0", {"start": v(20.5, -16.68) * mm, "end": v(20.5, -19.68) * mm});
            skLineSegment(sketch, "E72.7.0.1", {"start": v(23, -16.68) * mm, "end": v(20.5, -16.68) * mm});
            skLineSegment(sketch, "E72.7.0.3", {"start": v(22.77, -19.68) * mm, "end": v(20.5, -19.68) * mm});
            skLineSegment(sketch, "E72.7.1.0", {"start": v(20.5, -10.68) * mm, "end": v(20.5, -13.68) * mm});
            skLineSegment(sketch, "E72.7.1.1", {"start": v(23, -10.68) * mm, "end": v(20.5, -10.68) * mm});
            skLineSegment(sketch, "E72.7.1.3", {"start": v(23, -13.68) * mm, "end": v(20.5, -13.68) * mm});
            skLineSegment(sketch, "E72.7.2.0", {"start": v(20.5, -4.68) * mm, "end": v(20.5, -7.68) * mm});
            skLineSegment(sketch, "E72.7.2.1", {"start": v(23, -4.68) * mm, "end": v(20.5, -4.68) * mm});
            skLineSegment(sketch, "E72.7.2.3", {"start": v(23, -7.68) * mm, "end": v(20.5, -7.68) * mm});
            skLineSegment(sketch, "E72.7.3.0", {"start": v(20.5, 1.32) * mm, "end": v(20.5, -1.68) * mm});
            skLineSegment(sketch, "E72.7.3.1", {"start": v(23, 1.32) * mm, "end": v(20.5, 1.32) * mm});
            skLineSegment(sketch, "E72.7.3.3", {"start": v(23, -1.68) * mm, "end": v(20.5, -1.68) * mm});
            skLineSegment(sketch, "E72.7.4.0", {"start": v(20.5, 7.32) * mm, "end": v(20.5, 4.32) * mm});
            skLineSegment(sketch, "E72.7.4.1", {"start": v(23, 7.32) * mm, "end": v(20.5, 7.32) * mm});
            skLineSegment(sketch, "E72.7.4.3", {"start": v(23, 4.32) * mm, "end": v(20.5, 4.32) * mm});
            skLineSegment(sketch, "E72.7.5.0", {"start": v(20.5, 13.32) * mm, "end": v(20.5, 10.32) * mm});
            skLineSegment(sketch, "E72.7.5.1", {"start": v(23, 13.32) * mm, "end": v(20.5, 13.32) * mm});
            skLineSegment(sketch, "E72.7.5.3", {"start": v(23, 10.32) * mm, "end": v(20.5, 10.32) * mm});
            skLineSegment(sketch, "E72.7.6.0", {"start": v(20.5, 19.32) * mm, "end": v(20.5, 16.32) * mm});
            skLineSegment(sketch, "E72.7.6.1", {"start": v(22.37, 19.32) * mm, "end": v(20.5, 19.32) * mm});
            skLineSegment(sketch, "E72.7.6.3", {"start": v(23, 16.32) * mm, "end": v(20.5, 16.32) * mm});
            skLineSegment(sketch, "E72.direction1", {"start": v(-21.5, -19.68) * mm, "end": v(-15.5, -19.68) * mm, "construction": true});
            skLineSegment(sketch, "E72.direction2", {"start": v(-21.5, -19.68) * mm, "end": v(-21.5, -13.68) * mm, "construction": true});
            skPoint(sketch, "E73.orphan", {"position": v(23.5, -16.68) * mm});
            skPoint(sketch, "E74.orphan", {"position": v(23.5, -19.68) * mm});
            skPoint(sketch, "E75.orphan", {"position": v(23.5, -10.68) * mm});
            skPoint(sketch, "E76.orphan", {"position": v(23.5, -4.68) * mm});
            skPoint(sketch, "E77.orphan", {"position": v(23.5, 7.32) * mm});
            skPoint(sketch, "E78.orphan", {"position": v(23.5, 4.32) * mm});
            skPoint(sketch, "E79.orphan", {"position": v(23.5, 10.32) * mm});
            skPoint(sketch, "E80.orphan", {"position": v(23.5, 16.32) * mm});
            skPoint(sketch, "E81.orphan", {"position": v(23.5, 13.32) * mm});
            skPoint(sketch, "E82.orphan", {"position": v(23.5, 1.32) * mm});
            const initialGuessF4  = {"E70.0.1": [0.018, -0.01818460883017219, 0, 1, 0.005009362330054526, 0.005, 3.141592653589793, 4.71238898038469], "E70.0.3": [0.018, 0.016880927480209466, 0, 1, 0.005009362330054523, 0.005, 4.71238898038469, 0], "E70.0.5": [-0.02, 0.016880927480209463, 0, 1, 0.005009362330054526, 0.005, 0, 1.5707963267948963], "E70.0.7": [-0.02, -0.0181846088301722, 0, 1, 0.005009362330054523, 0.005, 1.5707963267948963, 3.141592653589793]};
            skSetInitialGuess(sketch, initialGuessF4);
            skSolve(sketch);
        }
        {
            var Q0;
            Q0=makeQuery(id+"F4.imprint","IMPRINT",FACE,{"disambiguationData":[TD([[makeQuery(id+"F4.imprint","IMPRINT",EDGE,{"derivedFrom":sQuery(id+"F4.wireOp",EDGE,"E72.0.6.0")}),1.0]])]});
            var Q1;
            Q1=makeQuery(id+"F4.imprint","IMPRINT",FACE,{"disambiguationData":[TD([[makeQuery(id+"F4.imprint","IMPRINT",EDGE,{"derivedFrom":sQuery(id+"F4.wireOp",EDGE,"E72.1.6.0")}),1.0]])]});
            var Q2;
            Q2=makeQuery(id+"F4.imprint","IMPRINT",FACE,{"disambiguationData":[TD([[makeQuery(id+"F4.imprint","IMPRINT",EDGE,{"derivedFrom":sQuery(id+"F4.wireOp",EDGE,"E72.2.6.0")}),1.0]])]});
            var Q3;
            Q3=makeQuery(id+"F4.imprint","IMPRINT",FACE,{"disambiguationData":[TD([[makeQuery(id+"F4.imprint","IMPRINT",EDGE,{"derivedFrom":sQuery(id+"F4.wireOp",EDGE,"E72.3.6.0")}),1.0]])]});
            var Q4;
            Q4=makeQuery(id+"F4.imprint","IMPRINT",FACE,{"disambiguationData":[TD([[makeQuery(id+"F4.imprint","IMPRINT",EDGE,{"derivedFrom":sQuery(id+"F4.wireOp",EDGE,"E72.4.6.0")}),1.0]])]});
            var Q5;
            Q5=makeQuery(id+"F4.imprint","IMPRINT",FACE,{"disambiguationData":[TD([[makeQuery(id+"F4.imprint","IMPRINT",EDGE,{"derivedFrom":sQuery(id+"F4.wireOp",EDGE,"E72.5.6.0")}),1.0]])]});
            var Q6;
            Q6=makeQuery(id+"F4.imprint","IMPRINT",FACE,{"disambiguationData":[TD([[makeQuery(id+"F4.imprint","IMPRINT",EDGE,{"derivedFrom":sQuery(id+"F4.wireOp",EDGE,"E72.6.6.0")}),1.0]])]});
            var Q7;
            Q7=makeQuery(id+"F4.imprint","IMPRINT",FACE,{"disambiguationData":[TD([[makeQuery(id+"F4.imprint","IMPRINT",EDGE,{"derivedFrom":sQuery(id+"F4.wireOp",EDGE,"E72.7.6.0")}),1.0]])]});
            var Q8;
            Q8=makeQuery(id+"F4.imprint","IMPRINT",FACE,{"disambiguationData":[TD([[makeQuery(id+"F4.imprint","IMPRINT",EDGE,{"derivedFrom":sQuery(id+"F4.wireOp",EDGE,"E72.7.5.0")}),1.0]])]});
            var Q9;
            Q9=makeQuery(id+"F4.imprint","IMPRINT",FACE,{"disambiguationData":[TD([[makeQuery(id+"F4.imprint","IMPRINT",EDGE,{"derivedFrom":sQuery(id+"F4.wireOp",EDGE,"E72.6.5.0")}),1.0]])]});
            var Q10;
            Q10=makeQuery(id+"F4.imprint","IMPRINT",FACE,{"disambiguationData":[TD([[makeQuery(id+"F4.imprint","IMPRINT",EDGE,{"derivedFrom":sQuery(id+"F4.wireOp",EDGE,"E72.5.5.0")}),1.0]])]});
            var Q11;
            Q11=makeQuery(id+"F4.imprint","IMPRINT",FACE,{"disambiguationData":[TD([[makeQuery(id+"F4.imprint","IMPRINT",EDGE,{"derivedFrom":sQuery(id+"F4.wireOp",EDGE,"E72.4.5.0")}),1.0]])]});
            var Q12;
            Q12=makeQuery(id+"F4.imprint","IMPRINT",FACE,{"disambiguationData":[TD([[makeQuery(id+"F4.imprint","IMPRINT",EDGE,{"derivedFrom":sQuery(id+"F4.wireOp",EDGE,"E72.3.5.0")}),1.0]])]});
            var Q13;
            Q13=makeQuery(id+"F4.imprint","IMPRINT",FACE,{"disambiguationData":[TD([[makeQuery(id+"F4.imprint","IMPRINT",EDGE,{"derivedFrom":sQuery(id+"F4.wireOp",EDGE,"E72.2.5.0")}),1.0]])]});
            var Q14;
            Q14=makeQuery(id+"F4.imprint","IMPRINT",FACE,{"disambiguationData":[TD([[makeQuery(id+"F4.imprint","IMPRINT",EDGE,{"derivedFrom":sQuery(id+"F4.wireOp",EDGE,"E72.1.5.0")}),1.0]])]});
            var Q15;
            Q15=makeQuery(id+"F4.imprint","IMPRINT",FACE,{"disambiguationData":[TD([[makeQuery(id+"F4.imprint","IMPRINT",EDGE,{"derivedFrom":sQuery(id+"F4.wireOp",EDGE,"E72.0.5.0")}),1.0]])]});
            var Q16;
            Q16=makeQuery(id+"F4.imprint","IMPRINT",FACE,{"disambiguationData":[TD([[makeQuery(id+"F4.imprint","IMPRINT",EDGE,{"derivedFrom":sQuery(id+"F4.wireOp",EDGE,"E72.0.4.0")}),1.0]])]});
            var Q17;
            Q17=makeQuery(id+"F4.imprint","IMPRINT",FACE,{"disambiguationData":[TD([[makeQuery(id+"F4.imprint","IMPRINT",EDGE,{"derivedFrom":sQuery(id+"F4.wireOp",EDGE,"E72.1.4.0")}),1.0]])]});
            var Q18;
            Q18=makeQuery(id+"F4.imprint","IMPRINT",FACE,{"disambiguationData":[TD([[makeQuery(id+"F4.imprint","IMPRINT",EDGE,{"derivedFrom":sQuery(id+"F4.wireOp",EDGE,"E72.2.4.0")}),1.0]])]});
            var Q19;
            Q19=makeQuery(id+"F4.imprint","IMPRINT",FACE,{"disambiguationData":[TD([[makeQuery(id+"F4.imprint","IMPRINT",EDGE,{"derivedFrom":sQuery(id+"F4.wireOp",EDGE,"E72.3.4.0")}),1.0]])]});
            var Q20;
            Q20=makeQuery(id+"F4.imprint","IMPRINT",FACE,{"disambiguationData":[TD([[makeQuery(id+"F4.imprint","IMPRINT",EDGE,{"derivedFrom":sQuery(id+"F4.wireOp",EDGE,"E72.4.4.0")}),1.0]])]});
            var Q21;
            Q21=makeQuery(id+"F4.imprint","IMPRINT",FACE,{"disambiguationData":[TD([[makeQuery(id+"F4.imprint","IMPRINT",EDGE,{"derivedFrom":sQuery(id+"F4.wireOp",EDGE,"E72.5.4.0")}),1.0]])]});
            var Q22;
            Q22=makeQuery(id+"F4.imprint","IMPRINT",FACE,{"disambiguationData":[TD([[makeQuery(id+"F4.imprint","IMPRINT",EDGE,{"derivedFrom":sQuery(id+"F4.wireOp",EDGE,"E72.6.4.0")}),1.0]])]});
            var Q23;
            Q23=makeQuery(id+"F4.imprint","IMPRINT",FACE,{"disambiguationData":[TD([[makeQuery(id+"F4.imprint","IMPRINT",EDGE,{"derivedFrom":sQuery(id+"F4.wireOp",EDGE,"E72.7.4.0")}),1.0]])]});
            var Q24;
            Q24=makeQuery(id+"F4.imprint","IMPRINT",FACE,{"disambiguationData":[TD([[makeQuery(id+"F4.imprint","IMPRINT",EDGE,{"derivedFrom":sQuery(id+"F4.wireOp",EDGE,"E72.7.3.0")}),1.0]])]});
            var Q25;
            Q25=makeQuery(id+"F4.imprint","IMPRINT",FACE,{"disambiguationData":[TD([[makeQuery(id+"F4.imprint","IMPRINT",EDGE,{"derivedFrom":sQuery(id+"F4.wireOp",EDGE,"E72.6.3.0")}),1.0]])]});
            var Q26;
            Q26=makeQuery(id+"F4.imprint","IMPRINT",FACE,{"disambiguationData":[TD([[makeQuery(id+"F4.imprint","IMPRINT",EDGE,{"derivedFrom":sQuery(id+"F4.wireOp",EDGE,"E72.5.3.0")}),1.0]])]});
            var Q27;
            Q27=makeQuery(id+"F4.imprint","IMPRINT",FACE,{"disambiguationData":[TD([[makeQuery(id+"F4.imprint","IMPRINT",EDGE,{"derivedFrom":sQuery(id+"F4.wireOp",EDGE,"E72.4.3.0")}),1.0]])]});
            var Q28;
            Q28=makeQuery(id+"F4.imprint","IMPRINT",FACE,{"disambiguationData":[TD([[makeQuery(id+"F4.imprint","IMPRINT",EDGE,{"derivedFrom":sQuery(id+"F4.wireOp",EDGE,"E72.3.3.0")}),1.0]])]});
            var Q29;
            Q29=makeQuery(id+"F4.imprint","IMPRINT",FACE,{"disambiguationData":[TD([[makeQuery(id+"F4.imprint","IMPRINT",EDGE,{"derivedFrom":sQuery(id+"F4.wireOp",EDGE,"E72.2.3.0")}),1.0]])]});
            var Q30;
            Q30=makeQuery(id+"F4.imprint","IMPRINT",FACE,{"disambiguationData":[TD([[makeQuery(id+"F4.imprint","IMPRINT",EDGE,{"derivedFrom":sQuery(id+"F4.wireOp",EDGE,"E72.1.3.0")}),1.0]])]});
            var Q31;
            Q31=makeQuery(id+"F4.imprint","IMPRINT",FACE,{"disambiguationData":[TD([[makeQuery(id+"F4.imprint","IMPRINT",EDGE,{"derivedFrom":sQuery(id+"F4.wireOp",EDGE,"E72.0.3.0")}),1.0]])]});
            var Q32;
            Q32=makeQuery(id+"F4.imprint","IMPRINT",FACE,{"disambiguationData":[TD([[makeQuery(id+"F4.imprint","IMPRINT",EDGE,{"derivedFrom":sQuery(id+"F4.wireOp",EDGE,"E72.0.2.0")}),1.0]])]});
            var Q33;
            Q33=makeQuery(id+"F4.imprint","IMPRINT",FACE,{"disambiguationData":[TD([[makeQuery(id+"F4.imprint","IMPRINT",EDGE,{"derivedFrom":sQuery(id+"F4.wireOp",EDGE,"E72.1.2.0")}),1.0]])]});
            var Q34;
            Q34=makeQuery(id+"F4.imprint","IMPRINT",FACE,{"disambiguationData":[TD([[makeQuery(id+"F4.imprint","IMPRINT",EDGE,{"derivedFrom":sQuery(id+"F4.wireOp",EDGE,"E72.2.2.0")}),1.0]])]});
            var Q35;
            Q35=makeQuery(id+"F4.imprint","IMPRINT",FACE,{"disambiguationData":[TD([[makeQuery(id+"F4.imprint","IMPRINT",EDGE,{"derivedFrom":sQuery(id+"F4.wireOp",EDGE,"E72.3.2.0")}),1.0]])]});
            var Q36;
            Q36=makeQuery(id+"F4.imprint","IMPRINT",FACE,{"disambiguationData":[TD([[makeQuery(id+"F4.imprint","IMPRINT",EDGE,{"derivedFrom":sQuery(id+"F4.wireOp",EDGE,"E72.4.2.0")}),1.0]])]});
            var Q37;
            Q37=makeQuery(id+"F4.imprint","IMPRINT",FACE,{"disambiguationData":[TD([[makeQuery(id+"F4.imprint","IMPRINT",EDGE,{"derivedFrom":sQuery(id+"F4.wireOp",EDGE,"E72.5.2.0")}),1.0]])]});
            var Q38;
            Q38=makeQuery(id+"F4.imprint","IMPRINT",FACE,{"disambiguationData":[TD([[makeQuery(id+"F4.imprint","IMPRINT",EDGE,{"derivedFrom":sQuery(id+"F4.wireOp",EDGE,"E72.6.2.0")}),1.0]])]});
            var Q39;
            Q39=makeQuery(id+"F4.imprint","IMPRINT",FACE,{"disambiguationData":[TD([[makeQuery(id+"F4.imprint","IMPRINT",EDGE,{"derivedFrom":sQuery(id+"F4.wireOp",EDGE,"E72.7.2.0")}),1.0]])]});
            var Q40;
            Q40=makeQuery(id+"F4.imprint","IMPRINT",FACE,{"disambiguationData":[TD([[makeQuery(id+"F4.imprint","IMPRINT",EDGE,{"derivedFrom":sQuery(id+"F4.wireOp",EDGE,"E72.7.1.0")}),1.0]])]});
            var Q41;
            Q41=makeQuery(id+"F4.imprint","IMPRINT",FACE,{"disambiguationData":[TD([[makeQuery(id+"F4.imprint","IMPRINT",EDGE,{"derivedFrom":sQuery(id+"F4.wireOp",EDGE,"E72.7.0.0")}),1.0]])]});
            var Q42;
            Q42=makeQuery(id+"F4.imprint","IMPRINT",FACE,{"disambiguationData":[TD([[makeQuery(id+"F4.imprint","IMPRINT",EDGE,{"derivedFrom":sQuery(id+"F4.wireOp",EDGE,"E72.6.1.0")}),1.0]])]});
            var Q43;
            Q43=makeQuery(id+"F4.imprint","IMPRINT",FACE,{"disambiguationData":[TD([[makeQuery(id+"F4.imprint","IMPRINT",EDGE,{"derivedFrom":sQuery(id+"F4.wireOp",EDGE,"E72.6.0.0")}),1.0]])]});
            var Q44;
            Q44=makeQuery(id+"F4.imprint","IMPRINT",FACE,{"disambiguationData":[TD([[makeQuery(id+"F4.imprint","IMPRINT",EDGE,{"derivedFrom":sQuery(id+"F4.wireOp",EDGE,"E72.5.0.0")}),1.0]])]});
            var Q45;
            Q45=makeQuery(id+"F4.imprint","IMPRINT",FACE,{"disambiguationData":[TD([[makeQuery(id+"F4.imprint","IMPRINT",EDGE,{"derivedFrom":sQuery(id+"F4.wireOp",EDGE,"E72.5.1.0")}),1.0]])]});
            var Q46;
            Q46=makeQuery(id+"F4.imprint","IMPRINT",FACE,{"disambiguationData":[TD([[makeQuery(id+"F4.imprint","IMPRINT",EDGE,{"derivedFrom":sQuery(id+"F4.wireOp",EDGE,"E72.4.1.0")}),1.0]])]});
            var Q47;
            Q47=makeQuery(id+"F4.imprint","IMPRINT",FACE,{"disambiguationData":[TD([[makeQuery(id+"F4.imprint","IMPRINT",EDGE,{"derivedFrom":sQuery(id+"F4.wireOp",EDGE,"E72.4.0.0")}),1.0]])]});
            var Q48;
            Q48=makeQuery(id+"F4.imprint","IMPRINT",FACE,{"disambiguationData":[TD([[makeQuery(id+"F4.imprint","IMPRINT",EDGE,{"derivedFrom":sQuery(id+"F4.wireOp",EDGE,"E72.3.0.0")}),1.0]])]});
            var Q49;
            Q49=makeQuery(id+"F4.imprint","IMPRINT",FACE,{"disambiguationData":[TD([[makeQuery(id+"F4.imprint","IMPRINT",EDGE,{"derivedFrom":sQuery(id+"F4.wireOp",EDGE,"E72.3.1.0")}),1.0]])]});
            var Q50;
            Q50=makeQuery(id+"F4.imprint","IMPRINT",FACE,{"disambiguationData":[TD([[makeQuery(id+"F4.imprint","IMPRINT",EDGE,{"derivedFrom":sQuery(id+"F4.wireOp",EDGE,"E72.2.1.0")}),1.0]])]});
            var Q51;
            Q51=makeQuery(id+"F4.imprint","IMPRINT",FACE,{"disambiguationData":[TD([[makeQuery(id+"F4.imprint","IMPRINT",EDGE,{"derivedFrom":sQuery(id+"F4.wireOp",EDGE,"E72.2.0.0")}),1.0]])]});
            var Q52;
            Q52=makeQuery(id+"F4.imprint","IMPRINT",FACE,{"disambiguationData":[TD([[makeQuery(id+"F4.imprint","IMPRINT",EDGE,{"derivedFrom":sQuery(id+"F4.wireOp",EDGE,"E72.1.0.0")}),1.0]])]});
            var Q53;
            Q53=makeQuery(id+"F4.imprint","IMPRINT",FACE,{"disambiguationData":[TD([[makeQuery(id+"F4.imprint","IMPRINT",EDGE,{"derivedFrom":sQuery(id+"F4.wireOp",EDGE,"E72.1.1.0")}),1.0]])]});
            var Q54;
            Q54=makeQuery(id+"F4.imprint","IMPRINT",FACE,{"disambiguationData":[TD([[makeQuery(id+"F4.imprint","IMPRINT",EDGE,{"derivedFrom":sQuery(id+"F4.wireOp",EDGE,"E72.0.1.0")}),1.0]])]});
            var Q55;
            Q55=makeQuery(id+"F4.imprint","IMPRINT",FACE,{"disambiguationData":[TD([[makeQuery(id+"F4.imprint","IMPRINT",EDGE,{"derivedFrom":sQuery(id+"F4.wireOp",EDGE,"E71.bottom")}),1.0]])]});
            extrude(context, id + "F5", {"entities" : qUnion([Q0, Q1, Q2, Q3, Q4, Q5, Q6, Q7, Q8, Q9, Q10, Q11, Q12, Q13, Q14, Q15, Q16, Q17, Q18, Q19, Q20, Q21, Q22, Q23, Q24, Q25, Q26, Q27, Q28, Q29, Q30, Q31, Q32, Q33, Q34, Q35, Q36, Q37, Q38, Q39, Q40, Q41, Q42, Q43, Q44, Q45, Q46, Q47, Q48, Q49, Q50, Q51, Q52, Q53, Q54, Q55]), "operationType" : NewBodyOperationType.REMOVE, "oppositeDirection" : true, "depth" : 25 * mm, "offsetDistance" : 25 * mm});
        }
        {
            var Q0;
            Q0=makeQuery(id+"F1.opExtrude","SWEPT_FACE",FACE,{"disambiguationData":[OSD([sQuery(id+"F0.wireOp",EDGE,"E0.top")])]});
            var sketch = newSketch(context, id + "F6", { "sketchPlane" : qUnion([Q0])});
            skLineSegment(sketch, "E83.0.0", {"start": v(25, 4) * mm, "end": v(-27, 4) * mm});
            skLineSegment(sketch, "E83.0.1", {"start": v(-27, 4) * mm, "end": v(-27, 0) * mm});
            skLineSegment(sketch, "E83.0.2", {"start": v(-27, 0) * mm, "end": v(25, 0) * mm});
            skLineSegment(sketch, "E83.0.3", {"start": v(25, 0) * mm, "end": v(25, 4) * mm});
            skArc(sketch, "E84", {"start": v(5, 4) * mm, "mid": v(0, 9) * mm, "end": v(-5, 4) * mm});
            skArc(sketch, "E85.0", {"start": v(3, 4) * mm, "mid": v(0, 7) * mm, "end": v(-3, 4) * mm});
            skSolve(sketch);
        }
        {
            var Q0;
            {var subQ0=sQuery(id+"F6.wireOp",EDGE,"E84");Q0=makeQuery(id+"F6.imprint","IMPRINT",FACE,{"disambiguationData":[TD([[makeQuery(id+"F6.imprint","IMPRINT",EDGE,{"derivedFrom":subQ0}),1.0]])]});}
            extrude(context, id + "F7", {"entities" : qUnion([Q0]), "operationType" : NewBodyOperationType.ADD, "oppositeDirection" : true, "depth" : 2 * mm, "offsetDistance" : 25 * mm});
        }
        {
            var Q0;
            Q0=makeQuery(id+"F1.opExtrude","CAP_EDGE",EDGE,{"disambiguationData":[OSD([sQuery(id+"F0.wireOp",EDGE,"E0.bottom")])],"isStart":false});
            var Q1;
            Q1=makeQuery(id+"F1.opExtrude","CAP_EDGE",EDGE,{"disambiguationData":[OSD([sQuery(id+"F0.wireOp",EDGE,"E0.left")])],"isStart":false});
            var Q2;
            {var subQ0=sQuery(id+"F0.wireOp",EDGE,"E0.left");var subQ2=sQuery(id+"F0.wireOp",EDGE,"E0.top");Q2=makeQuery(id+"F7.boolean.opBoolean","SPLIT",EDGE,{"disambiguationData":[TD([makeQuery(id+"F1.opExtrude","SWEPT_FACE",FACE,{"disambiguationData":[OSD([subQ0])]})])],"derivedFrom":makeQuery(id+"F1.opExtrude","CAP_EDGE",EDGE,{"disambiguationData":[OSD([subQ2])],"isStart":false})});}
            var Q3;
            {var subQ0=sQuery(id+"F0.wireOp",EDGE,"E0.right");var subQ1=sQuery(id+"F0.wireOp",EDGE,"E0.top");Q3=makeQuery(id+"F7.boolean.opBoolean","SPLIT",EDGE,{"disambiguationData":[TD([makeQuery(id+"F1.opExtrude","SWEPT_FACE",FACE,{"disambiguationData":[OSD([subQ0])]})])],"derivedFrom":makeQuery(id+"F1.opExtrude","CAP_EDGE",EDGE,{"disambiguationData":[OSD([subQ1])],"isStart":false})});}
            var Q4;
            Q4=makeQuery(id+"F1.opExtrude","CAP_EDGE",EDGE,{"disambiguationData":[OSD([sQuery(id+"F0.wireOp",EDGE,"E0.right")])],"isStart":false});
            fillet(context, id + "F8", {"entities" : qUnion([Q0, Q1, Q2, Q3, Q4]), "radius" : 1 * mm, "tangentPropagation" : true, "allowEdgeOverflow" : false});
        }
    });
